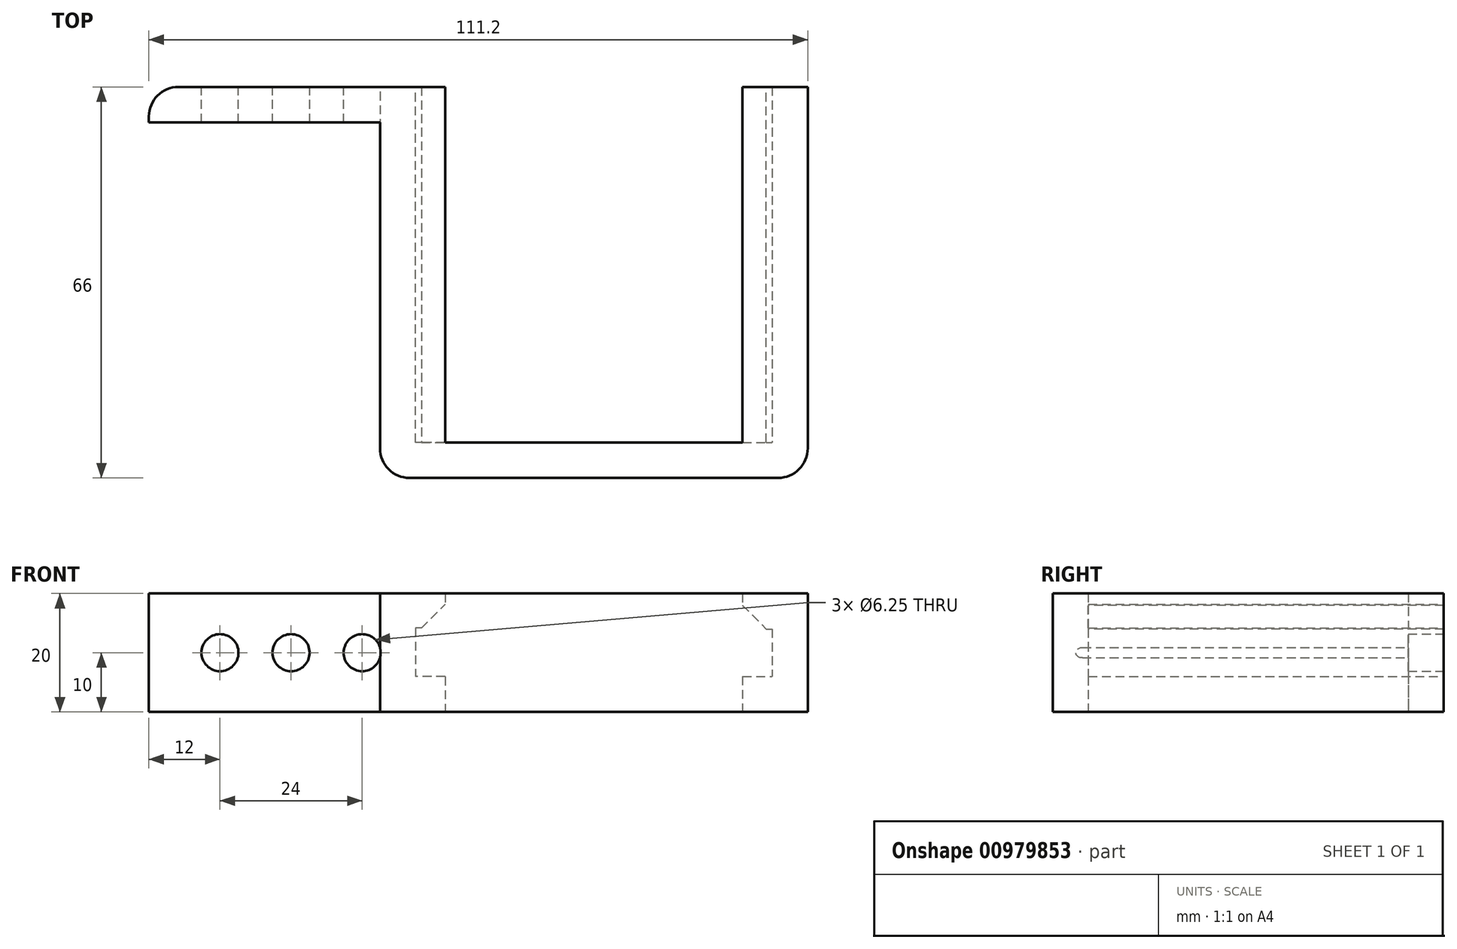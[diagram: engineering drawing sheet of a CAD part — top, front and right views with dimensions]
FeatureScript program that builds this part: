
annotation { "Feature Type Name" : "Feature", "Feature Type Description" : "" }
export const myFeature = defineFeature(function(context is Context, id is Id, definition is map)
    precondition{}
    {
        {
            var Q0;
            Q0=qCreatedBy(makeId("Top.planeOp"),FACE);
            var sketch = newSketch(context, id + "F0", { "sketchPlane" : qUnion([Q0])});
            skLineSegment(sketch, "E0", {"start": v(0, 0) * mm, "end": v(45, 0) * mm});
            skLineSegment(sketch, "E1", {"start": v(45, 0) * mm, "end": v(45, -60) * mm});
            skLineSegment(sketch, "E2", {"start": v(45, -60) * mm, "end": v(105.2, -60) * mm});
            skLineSegment(sketch, "E3", {"start": v(105.2, -60) * mm, "end": v(105.2, 0) * mm});
            skLineSegment(sketch, "E4", {"start": v(105.2, 0) * mm, "end": v(111.2, 0) * mm});
            skLineSegment(sketch, "E5", {"start": v(111.2, 0) * mm, "end": v(111.2, -66) * mm});
            skLineSegment(sketch, "E6", {"start": v(111.2, -66) * mm, "end": v(39, -66) * mm});
            skLineSegment(sketch, "E7", {"start": v(39, -66) * mm, "end": v(39, -6) * mm});
            skLineSegment(sketch, "E8", {"start": v(39, -6) * mm, "end": v(0, -6) * mm});
            skLineSegment(sketch, "E9", {"start": v(0, -6) * mm, "end": v(0, 0) * mm});
            skSolve(sketch);
        }
        {
            var Q0;
            Q0=makeQuery(id+"F0.imprint","IMPRINT",FACE,{"disambiguationData":[TD([[makeQuery(id+"F0.imprint","IMPRINT",EDGE,{"derivedFrom":sQuery(id+"F0.wireOp",EDGE,"E0")}),-1.0]])]});
            extrude(context, id + "F1", {"entities" : qUnion([Q0]), "depth" : 20 * mm, "offsetDistance" : 25 * mm});
        }
        {
            var Q0;
            Q0=makeQuery(id+"F1.opExtrude","SWEPT_FACE",FACE,{"disambiguationData":[OSD([sQuery(id+"F0.wireOp",EDGE,"E0")])]});
            var sketch = newSketch(context, id + "F2", { "sketchPlane" : qUnion([Q0])});
            skPoint(sketch, "E10", {"position": v(-12, 10) * mm});
            skPoint(sketch, "E11", {"position": v(-24, 10) * mm});
            skPoint(sketch, "E12", {"position": v(-36, 10) * mm});
            skSolve(sketch);
        }
        {
            var Q0;
            Q0=sQuery(id+"F2.wireOp",VERTEX,"E12");
            var Q1;
            Q1=sQuery(id+"F2.wireOp",VERTEX,"E11");
            var Q2;
            Q2=sQuery(id+"F2.wireOp",VERTEX,"E10");
            var Q3;
            Q3=makeQuery(id+"F1.opExtrude","SWEPT_BODY",BODY,{"disambiguationData":[OSD([sQuery(id+"F0.wireOp",EDGE,"E0"),sQuery(id+"F0.wireOp",EDGE,"E1"),sQuery(id+"F0.wireOp",EDGE,"E2"),sQuery(id+"F0.wireOp",EDGE,"E3"),sQuery(id+"F0.wireOp",EDGE,"E4"),sQuery(id+"F0.wireOp",EDGE,"E5"),sQuery(id+"F0.wireOp",EDGE,"E6"),sQuery(id+"F0.wireOp",EDGE,"E7"),sQuery(id+"F0.wireOp",EDGE,"E8"),sQuery(id+"F0.wireOp",EDGE,"E9")])]});
            hole(context, id + "F3", {"style" : HoleStyle.SIMPLE, "endStyle" : HoleEndStyle.THROUGH, "standardTappedOrClearance" : lookupTablePath({ "standard" : "ANSI", "size" : "D (0.25)", "type" : "Drilled" }), "standardBlindInLast" : lookupTablePath({ "standard" : "ANSI", "size" : "D (0.25)", "type" : "Drilled" }), "holeDiameter" : 6.25 * mm, "majorDiameter" : 4 * mm, "isTappedThrough" : true, "tappedDepth" : 12 * mm, "tapClearance" : 3, "locations" : qUnion([Q0, Q1, Q2]), "scope" : qUnion([Q3])});
        }
        {
            var Q0;
            Q0=makeQuery(id+"F1.opExtrude","SWEPT_FACE",FACE,{"disambiguationData":[OSD([sQuery(id+"F0.wireOp",EDGE,"E3")])]});
            var sketch = newSketch(context, id + "F4", { "sketchPlane" : qUnion([Q0])});
            skLineSegment(sketch, "E13", {"start": v(60, 6) * mm, "end": v(0, 6) * mm});
            skLineSegment(sketch, "E14", {"start": v(0, 14) * mm, "end": v(60, 14) * mm});
            skSolve(sketch);
        }
        {
            var Q0;
            Q0=makeQuery(id+"F1.opExtrude","SWEPT_FACE",FACE,{"disambiguationData":[OSD([sQuery(id+"F0.wireOp",EDGE,"E1")])]});
            var sketch = newSketch(context, id + "F5", { "sketchPlane" : qUnion([Q0])});
            skLineSegment(sketch, "E15", {"start": v(-60, 14.15) * mm, "end": v(0, 14.15) * mm});
            skLineSegment(sketch, "E16", {"start": v(-60, 5.96) * mm, "end": v(0, 5.96) * mm});
            skSolve(sketch);
        }
        {
            var Q0;
            {var subQ0=sQuery(id+"F4.wireOp",EDGE,"E14");Q0=makeQuery(id+"F4.imprint","IMPRINT",FACE,{"disambiguationData":[TD([[makeQuery(id+"F4.imprint","IMPRINT",EDGE,{"derivedFrom":subQ0}),1.0]])]});}
            var Q1;
            {var subQ0=sQuery(id+"F4.wireOp",EDGE,"E13");Q1=makeQuery(id+"F4.imprint","IMPRINT",FACE,{"disambiguationData":[TD([[makeQuery(id+"F4.imprint","IMPRINT",EDGE,{"derivedFrom":subQ0}),1.0]])]});}
            extrude(context, id + "F6", {"entities" : qUnion([Q0, Q1]), "operationType" : NewBodyOperationType.ADD, "depth" : 5 * mm, "offsetDistance" : 25 * mm});
        }
        {
            var Q0;
            {var subQ0=sQuery(id+"F5.wireOp",EDGE,"E15");Q0=makeQuery(id+"F5.imprint","IMPRINT",FACE,{"disambiguationData":[TD([[makeQuery(id+"F5.imprint","IMPRINT",EDGE,{"derivedFrom":subQ0}),1.0]])]});}
            var Q1;
            {var subQ0=sQuery(id+"F5.wireOp",EDGE,"E16");Q1=makeQuery(id+"F5.imprint","IMPRINT",FACE,{"disambiguationData":[TD([[makeQuery(id+"F5.imprint","IMPRINT",EDGE,{"derivedFrom":subQ0}),-1.0]])]});}
            extrude(context, id + "F7", {"entities" : qUnion([Q0, Q1]), "operationType" : NewBodyOperationType.ADD, "depth" : 5 * mm, "offsetDistance" : 25 * mm});
        }
        {
            var Q0;
            Q0=makeQuery(id+"F7.opExtrude","CAP_EDGE",EDGE,{"disambiguationData":[OSD([sQuery(id+"F5.wireOp",EDGE,"E15")])],"isStart":false});
            var Q1;
            Q1=makeQuery(id+"F6.opExtrude","CAP_EDGE",EDGE,{"disambiguationData":[OSD([sQuery(id+"F4.wireOp",EDGE,"E14")])],"isStart":false});
            chamfer(context, id + "F8", {"entities" : qUnion([Q0, Q1]), "width" : 4 * mm, "tangentPropagation" : true});
        }
        {
            var Q0;
            Q0=makeQuery(id+"F1.opExtrude","SWEPT_EDGE",EDGE,{"disambiguationData":[OSD([sQuery(id+"F0.wireOp",EDGE,"E5"),sQuery(id+"F0.wireOp",EDGE,"E6")])]});
            var Q1;
            {var subQ0=sQuery(id+"F0.wireOp",EDGE,"E7");var subQ1=sQuery(id+"F0.wireOp",EDGE,"E6");Q1=makeQuery(id+"F3.hole-0.boolean.opBoolean","SPLIT",EDGE,{"disambiguationData":[TD([makeQuery(id+"F1.opExtrude","CAP_FACE",FACE,{"disambiguationData":[OSD([sQuery(id+"F0.wireOp",EDGE,"E0"),sQuery(id+"F0.wireOp",EDGE,"E1"),sQuery(id+"F0.wireOp",EDGE,"E2"),sQuery(id+"F0.wireOp",EDGE,"E3"),sQuery(id+"F0.wireOp",EDGE,"E4"),sQuery(id+"F0.wireOp",EDGE,"E5"),subQ1,subQ0,sQuery(id+"F0.wireOp",EDGE,"E8"),sQuery(id+"F0.wireOp",EDGE,"E9")])],"isStart":false})])],"derivedFrom":makeQuery(id+"F1.opExtrude","SWEPT_EDGE",EDGE,{"disambiguationData":[OSD([subQ1,subQ0])]})});}
            var Q2;
            {var subQ0=sQuery(id+"F0.wireOp",EDGE,"E7");var subQ1=sQuery(id+"F0.wireOp",EDGE,"E6");Q2=makeQuery(id+"F3.hole-0.boolean.opBoolean","SPLIT",EDGE,{"disambiguationData":[TD([makeQuery(id+"F1.opExtrude","CAP_FACE",FACE,{"disambiguationData":[OSD([sQuery(id+"F0.wireOp",EDGE,"E0"),sQuery(id+"F0.wireOp",EDGE,"E1"),sQuery(id+"F0.wireOp",EDGE,"E2"),sQuery(id+"F0.wireOp",EDGE,"E3"),sQuery(id+"F0.wireOp",EDGE,"E4"),sQuery(id+"F0.wireOp",EDGE,"E5"),subQ1,subQ0,sQuery(id+"F0.wireOp",EDGE,"E8"),sQuery(id+"F0.wireOp",EDGE,"E9")])],"isStart":true})])],"derivedFrom":makeQuery(id+"F1.opExtrude","SWEPT_EDGE",EDGE,{"disambiguationData":[OSD([subQ1,subQ0])]})});}
            var Q3;
            Q3=makeQuery(id+"F1.opExtrude","SWEPT_EDGE",EDGE,{"disambiguationData":[OSD([sQuery(id+"F0.wireOp",EDGE,"E0"),sQuery(id+"F0.wireOp",EDGE,"E9")])]});
            fillet(context, id + "F9", {"entities" : qUnion([Q0, Q1, Q2, Q3]), "radius" : 5 * mm, "tangentPropagation" : true, "allowEdgeOverflow" : false});
        }
    });
